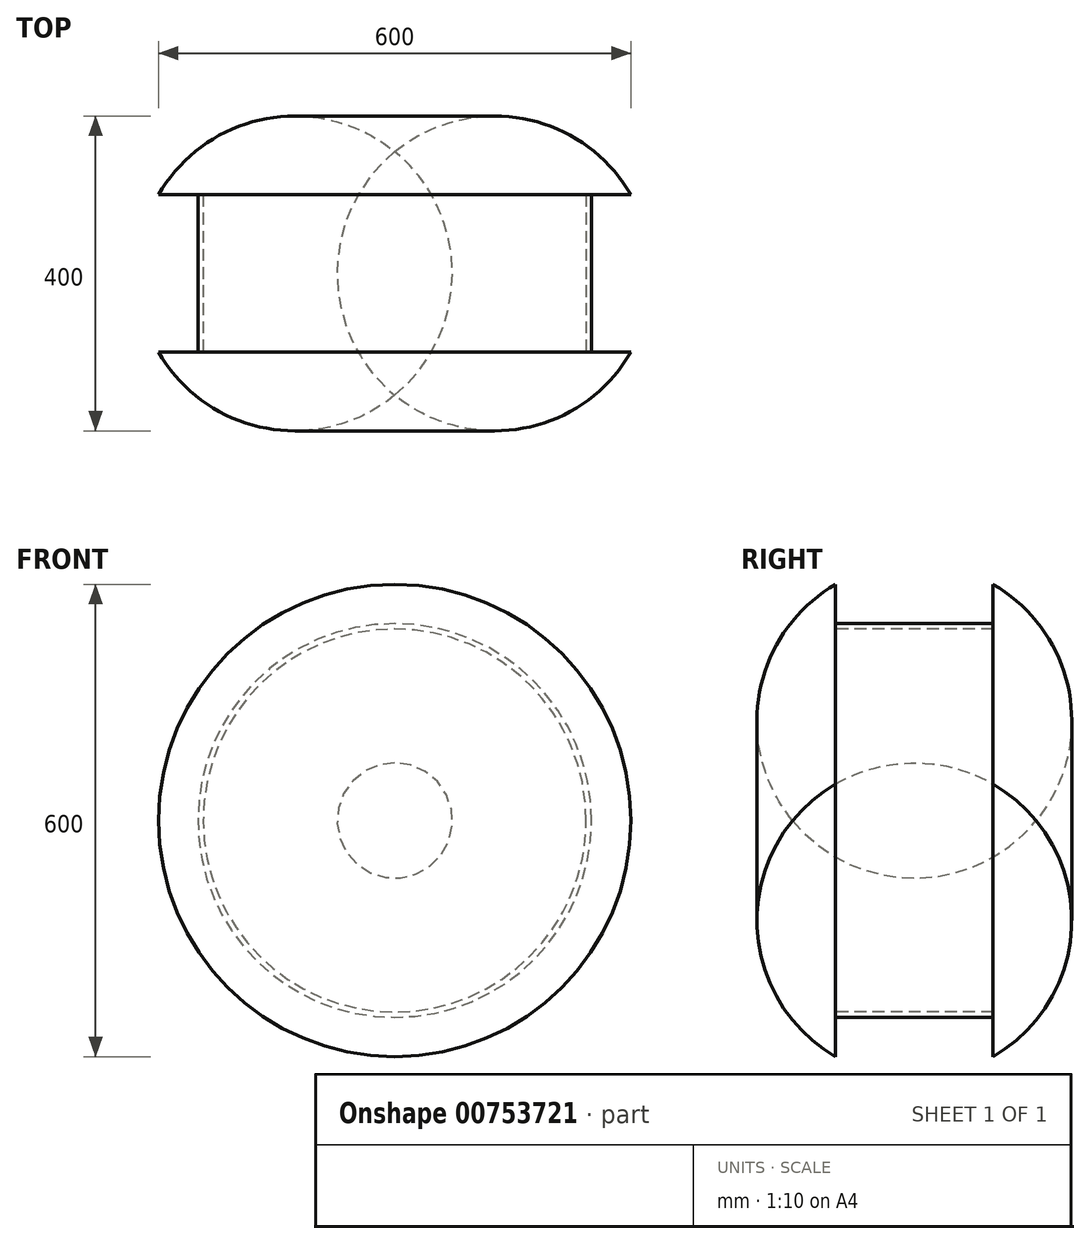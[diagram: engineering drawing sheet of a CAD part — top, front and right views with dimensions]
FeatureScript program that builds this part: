
annotation { "Feature Type Name" : "Feature", "Feature Type Description" : "" }
export const myFeature = defineFeature(function(context is Context, id is Id, definition is map)
    precondition{}
    {
        {
            var Q0;
            Q0=qCreatedBy(makeId("Top.planeOp"),FACE);
            var sketch = newSketch(context, id + "F0", { "sketchPlane" : qUnion([Q0])});
            skLineSegment(sketch, "E0", {"start": v(250, 100) * mm, "end": v(300, 100) * mm});
            skLineSegment(sketch, "E1", {"start": v(250, -100) * mm, "end": v(300, -100) * mm});
            skLineSegment(sketch, "E2", {"start": v(250, -100) * mm, "end": v(250, 100) * mm});
            skLineSegment(sketch, "E3", {"start": v(0, 0) * mm, "end": v(0, 11.02) * mm});
            skArc(sketch, "E4", {"start": v(300, -100) * mm, "mid": v(326.8, 0) * mm, "end": v(300, 100) * mm});
            skLineSegment(sketch, "E5.left", {"start": v(250, 100) * mm, "end": v(250, -100) * mm});
            skLineSegment(sketch, "E5.right", {"start": v(0, 100) * mm, "end": v(0, 0) * mm});
            skLineSegment(sketch, "E6.right", {"start": v(0, -100) * mm, "end": v(0, 100) * mm});
            skSolve(sketch);
        }
        {
            var Q0;
            Q0=makeQuery(id+"F0.imprint","IMPRINT",FACE,{"disambiguationData":[TD([[makeQuery(id+"F0.imprint","IMPRINT",EDGE,{"derivedFrom":sQuery(id+"F0.wireOp",EDGE,"E0")}),-1.0]])]});
            var Q1;
            Q1=sQuery(id+"F0.wireOp",EDGE,"E3");
            revolve(context, id + "F1", {"surfaceOperationType" : NewSurfaceOperationType.NEW, "entities" : qUnion([Q0]), "axis" : qUnion([Q1]), "revolveType" : RevolveType.FULL});
        }
        {
            var Q0;
            Q0=qCreatedBy(makeId("Top.planeOp"),FACE);
            var sketch = newSketch(context, id + "F2", { "sketchPlane" : qUnion([Q0])});
            skLineSegment(sketch, "E7.bottom", {"start": v(0, 100.02) * mm, "end": v(243.2, 100.02) * mm});
            skLineSegment(sketch, "E7.top", {"start": v(0, -99.98) * mm, "end": v(243.2, -99.98) * mm});
            skLineSegment(sketch, "E7.right", {"start": v(243.2, 100.02) * mm, "end": v(243.2, -99.98) * mm});
            skLineSegment(sketch, "E8", {"start": v(0, 100.02) * mm, "end": v(0, -99.98) * mm});
            skPoint(sketch, "E9.orphan", {"position": v(-6.8, 100.02) * mm});
            skPoint(sketch, "E10.orphan", {"position": v(-6.8, -99.98) * mm});
            skSolve(sketch);
        }
        {
            var Q0;
            Q0=makeQuery(id+"F2.imprint","IMPRINT",FACE,{"disambiguationData":[TD([[makeQuery(id+"F2.imprint","IMPRINT",EDGE,{"derivedFrom":sQuery(id+"F2.wireOp",EDGE,"E7.bottom")}),-1.0]])]});
            var Q1;
            Q1=sQuery(id+"F0.wireOp",EDGE,"E6.right");
            revolve(context, id + "F3", {"surfaceOperationType" : NewSurfaceOperationType.NEW, "entities" : qUnion([Q0]), "axis" : qUnion([Q1]), "revolveType" : RevolveType.FULL});
        }
    });
